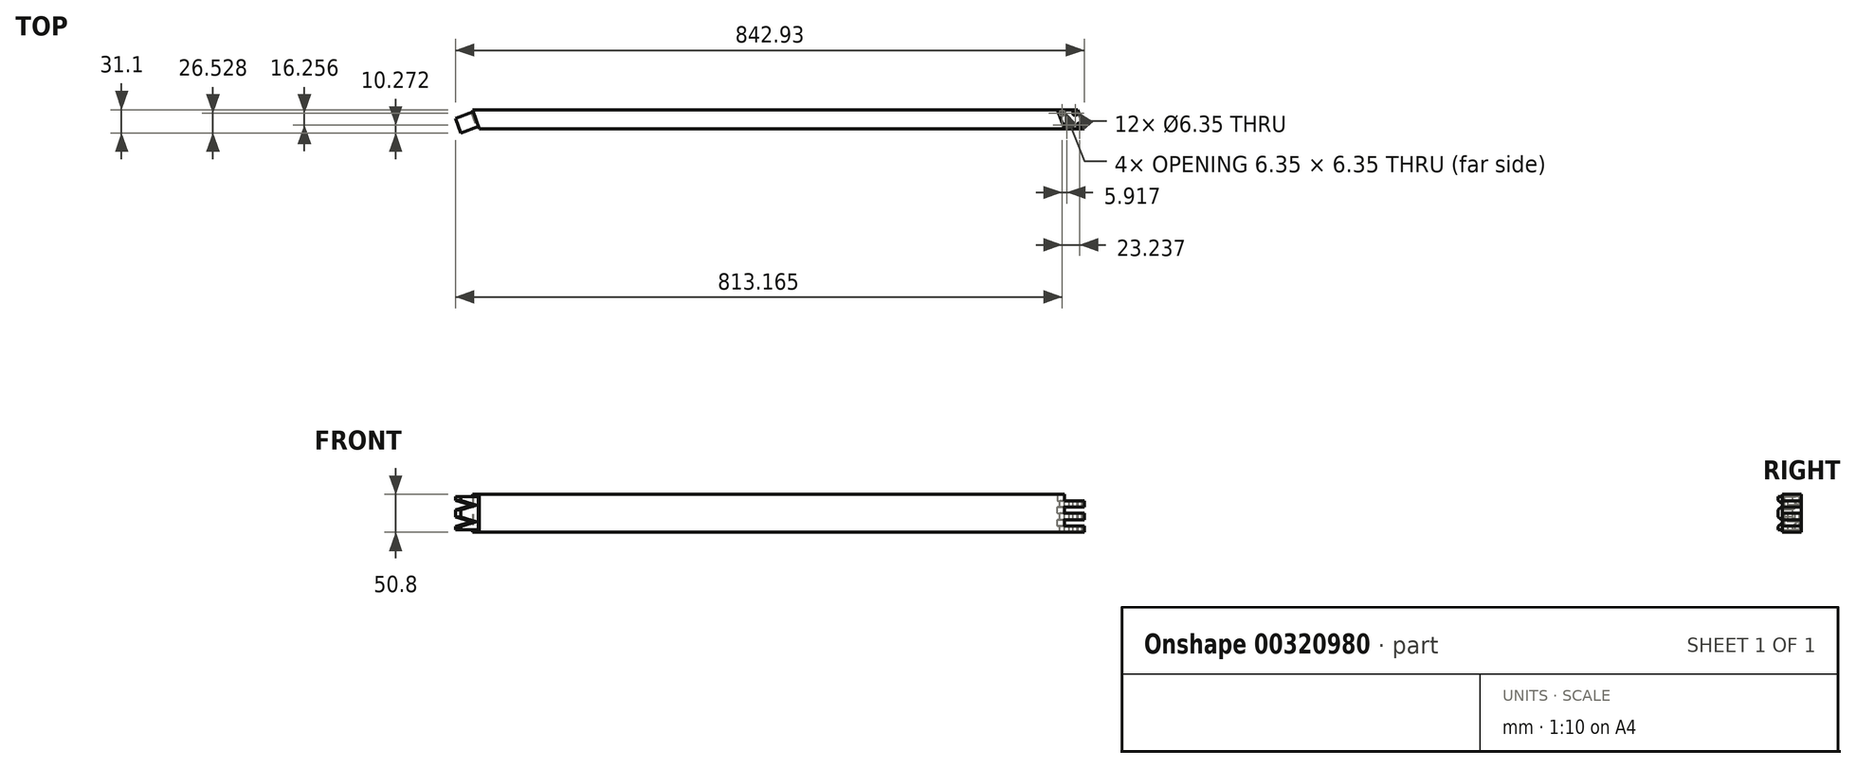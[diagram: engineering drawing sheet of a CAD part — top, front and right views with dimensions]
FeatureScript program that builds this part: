
annotation { "Feature Type Name" : "Feature", "Feature Type Description" : "" }
export const myFeature = defineFeature(function(context is Context, id is Id, definition is map)
    precondition{}
    {
        {
            var Q0;
            Q0=qCreatedBy(makeId("Top.planeOp"),FACE);
            var sketch = newSketch(context, id + "F0", { "sketchPlane" : qUnion([Q0])});
            skLineSegment(sketch, "E0", {"start": v(-414.7, 12.7) * mm, "end": v(-405.45, -12.7) * mm});
            skLineSegment(sketch, "E1", {"start": v(-405.45, -12.7) * mm, "end": v(405.45, -12.7) * mm});
            skLineSegment(sketch, "E2", {"start": v(405.45, -12.7) * mm, "end": v(396.2, 12.7) * mm});
            skLineSegment(sketch, "E3", {"start": v(396.2, 12.7) * mm, "end": v(-414.7, 12.7) * mm});
            skLineSegment(sketch, "E4", {"start": v(369.18, 12.7) * mm, "end": v(378.42, -12.7) * mm, "construction": true});
            skLineSegment(sketch, "E5", {"start": v(-387.67, 12.7) * mm, "end": v(-378.42, -12.7) * mm, "construction": true});
            skSolve(sketch);
        }
        {
            var Q0;
            Q0=makeQuery(id+"F0.imprint","IMPRINT",FACE,{"disambiguationData":[TD([[makeQuery(id+"F0.imprint","IMPRINT",EDGE,{"derivedFrom":sQuery(id+"F0.wireOp",EDGE,"E0")}),1.0]])]});
            extrude(context, id + "F1", {"entities" : qUnion([Q0]), "depth" : 50.8 * mm});
        }
        {
            var Q0;
            Q0=makeQuery(id+"F1.opExtrude","SWEPT_FACE",FACE,{"disambiguationData":[OSD([sQuery(id+"F0.wireOp",EDGE,"E3")])]});
            var sketch = newSketch(context, id + "F2", { "sketchPlane" : qUnion([Q0])});
            skLineSegment(sketch, "E6", {"start": v(-396.2, 8.47) * mm, "end": v(-369.16, 8.47) * mm});
            skLineSegment(sketch, "E7", {"start": v(-369.16, 8.47) * mm, "end": v(-369.16, 0) * mm});
            skLineSegment(sketch, "E8", {"start": v(-369.16, 0) * mm, "end": v(-396.2, 0) * mm});
            skLineSegment(sketch, "E9", {"start": v(-396.2, 0) * mm, "end": v(-396.2, 8.47) * mm});
            skLineSegment(sketch, "E10", {"start": v(-396.2, 16.93) * mm, "end": v(-369.16, 16.93) * mm});
            skLineSegment(sketch, "E11", {"start": v(-369.16, 16.93) * mm, "end": v(-369.16, 25.4) * mm});
            skLineSegment(sketch, "E12", {"start": v(-369.16, 25.4) * mm, "end": v(-396.2, 25.4) * mm});
            skLineSegment(sketch, "E13", {"start": v(-396.2, 25.4) * mm, "end": v(-396.2, 16.93) * mm});
            skLineSegment(sketch, "E14", {"start": v(-396.2, 33.87) * mm, "end": v(-369.16, 33.87) * mm});
            skLineSegment(sketch, "E15", {"start": v(-369.16, 33.87) * mm, "end": v(-369.16, 42.33) * mm});
            skLineSegment(sketch, "E16", {"start": v(-369.16, 42.33) * mm, "end": v(-396.2, 42.33) * mm});
            skLineSegment(sketch, "E17", {"start": v(-396.2, 42.33) * mm, "end": v(-396.2, 33.87) * mm});
            skLineSegment(sketch, "E18", {"start": v(-369.16, 8.47) * mm, "end": v(-369.16, 16.93) * mm});
            skLineSegment(sketch, "E19", {"start": v(-369.16, 25.4) * mm, "end": v(-369.16, 33.87) * mm});
            skLineSegment(sketch, "E20", {"start": v(-369.16, 50.8) * mm, "end": v(-369.16, 42.33) * mm});
            skSolve(sketch);
        }
        {
            var Q0;
            {var subQ0=sQuery(id+"F2.wireOp",EDGE,"E6");Q0=makeQuery(id+"F2.imprint","IMPRINT",FACE,{"disambiguationData":[TD([[makeQuery(id+"F2.imprint","IMPRINT",EDGE,{"derivedFrom":subQ0}),1.0]])]});}
            var Q1;
            {var subQ0=sQuery(id+"F2.wireOp",EDGE,"E12");Q1=makeQuery(id+"F2.imprint","IMPRINT",FACE,{"disambiguationData":[TD([[makeQuery(id+"F2.imprint","IMPRINT",EDGE,{"derivedFrom":subQ0}),-1.0]])]});}
            var Q2;
            {var subQ0=sQuery(id+"F2.wireOp",EDGE,"E16");Q2=makeQuery(id+"F2.imprint","IMPRINT",FACE,{"disambiguationData":[TD([[makeQuery(id+"F2.imprint","IMPRINT",EDGE,{"derivedFrom":subQ0}),-1.0]])]});}
            var Q3;
            Q3=makeQuery(id+"F1.opExtrude","CAP_EDGE",EDGE,{"disambiguationData":[OSD([sQuery(id+"F0.wireOp",EDGE,"E2")])],"isStart":false});
            sweep(context, id + "F3", {"operationType" : NewBodyOperationType.REMOVE, "profiles" : qUnion([Q0, Q1, Q2]), "path" : qUnion([Q3])});
        }
        {
            var Q0;
            Q0=makeQuery(id+"F1.opExtrude","CAP_FACE",FACE,{"disambiguationData":[OSD([sQuery(id+"F0.wireOp",EDGE,"E0"),sQuery(id+"F0.wireOp",EDGE,"E1"),sQuery(id+"F0.wireOp",EDGE,"E2"),sQuery(id+"F0.wireOp",EDGE,"E3")])],"isStart":false});
            var sketch = newSketch(context, id + "F4", { "sketchPlane" : qUnion([Q0])});
            skLineSegment(sketch, "E21", {"start": v(-405.45, -12.7) * mm, "end": v(-429.32, -21.39) * mm});
            skSolve(sketch);
        }
        {
            var Q0;
            Q0=makeQuery(id+"F1.opExtrude","SWEPT_FACE",FACE,{"disambiguationData":[OSD([sQuery(id+"F0.wireOp",EDGE,"E0")])]});
            var sketch = newSketch(context, id + "F5", { "sketchPlane" : qUnion([Q0])});
            skLineSegment(sketch, "E22.bottom", {"start": v(-129.91, 47.62) * mm, "end": v(-150.6, 47.62) * mm});
            skLineSegment(sketch, "E22.top", {"start": v(-129.91, 3.18) * mm, "end": v(-150.6, 3.18) * mm});
            skLineSegment(sketch, "E22.left", {"start": v(-129.91, 47.62) * mm, "end": v(-129.91, 3.18) * mm});
            skLineSegment(sketch, "E22.right", {"start": v(-150.6, 47.62) * mm, "end": v(-150.6, 3.18) * mm});
            skSolve(sketch);
        }
        {
            var Q0;
            Q0=makeQuery(id+"F5.imprint","IMPRINT",FACE,{"disambiguationData":[TD([[makeQuery(id+"F5.imprint","IMPRINT",EDGE,{"derivedFrom":sQuery(id+"F5.wireOp",EDGE,"E22.bottom")}),1.0]])]});
            var Q1;
            Q1=sQuery(id+"F4.wireOp",EDGE,"E21");
            sweep(context, id + "F6", {"operationType" : NewBodyOperationType.ADD, "profiles" : qUnion([Q0]), "path" : qUnion([Q1])});
        }
        {
            var Q0;
            Q0=makeQuery(id+"F6.opSweep","SWEPT_FACE",FACE,{"disambiguationData":[OSD([sQuery(id+"F4.wireOp",EDGE,"E21"),sQuery(id+"F5.wireOp",EDGE,"E22.left")])]});
            var sketch = newSketch(context, id + "F7", { "sketchPlane" : qUnion([Q0])});
            skLineSegment(sketch, "E23", {"start": v(-410.74, 42.86) * mm, "end": v(-388.52, 36.51) * mm});
            skLineSegment(sketch, "E24", {"start": v(-388.52, 36.51) * mm, "end": v(-410.74, 30.16) * mm});
            skLineSegment(sketch, "E25", {"start": v(-410.74, 30.16) * mm, "end": v(-410.74, 42.86) * mm});
            skLineSegment(sketch, "E26", {"start": v(-410.74, 25.4) * mm, "end": v(-382.98, 25.4) * mm, "construction": true});
            skPoint(sketch, "E26.endSnap0", {"position": v(-385.34, 25.4) * mm});
            skLineSegment(sketch, "E27.MirrorCS", {"start": v(-410.74, 20.64) * mm, "end": v(-410.74, 7.94) * mm});
            skLineSegment(sketch, "E28.MirrorCS", {"start": v(-388.52, 14.29) * mm, "end": v(-410.74, 20.64) * mm});
            skLineSegment(sketch, "E29.MirrorCS", {"start": v(-410.74, 7.94) * mm, "end": v(-388.52, 14.29) * mm});
            skSolve(sketch);
        }
        {
            var Q0;
            Q0=makeQuery(id+"F7.imprint","IMPRINT",FACE,{"disambiguationData":[TD([[makeQuery(id+"F7.imprint","IMPRINT",EDGE,{"derivedFrom":sQuery(id+"F7.wireOp",EDGE,"E23")}),-1.0]])]});
            var Q1;
            Q1=makeQuery(id+"F7.imprint","IMPRINT",FACE,{"disambiguationData":[TD([[makeQuery(id+"F7.imprint","IMPRINT",EDGE,{"derivedFrom":sQuery(id+"F7.wireOp",EDGE,"E27.MirrorCS")}),-1.0]])]});
            extrude(context, id + "F8", {"entities" : qUnion([Q0, Q1]), "operationType" : NewBodyOperationType.REMOVE, "endBound" : BoundingType.THROUGH_ALL, "oppositeDirection" : true, "depth" : 25.4 * mm});
        }
        {
            var Q0;
            Q0=makeQuery(id+"F3.boolean.opBoolean","COPY",FACE,{"derivedFrom":makeQuery(id+"F3.opSweep","SWEPT_FACE",FACE,{"disambiguationData":[OSD([sQuery(id+"F0.wireOp",EDGE,"E2"),sQuery(id+"F2.wireOp",EDGE,"E16")])]})});
            var sketch = newSketch(context, id + "F9", { "sketchPlane" : qUnion([Q0])});
            skLineSegment(sketch, "E30.0", {"start": v(398.92, -8.13) * mm, "end": v(393, 8.13) * mm, "construction": true});
            skLineSegment(sketch, "E30.1", {"start": v(381.6, -8.13) * mm, "end": v(398.92, -8.13) * mm, "construction": true});
            skLineSegment(sketch, "E30.2", {"start": v(375.69, 8.13) * mm, "end": v(381.6, -8.13) * mm, "construction": true});
            skLineSegment(sketch, "E30.3", {"start": v(393, 8.13) * mm, "end": v(375.69, 8.13) * mm, "construction": true});
            skCircle(sketch, "E31", {"center": v(393, 8.13) * mm, "radius": 3.18 * mm});
            skCircle(sketch, "E32", {"center": v(375.69, 8.13) * mm, "radius": 3.18 * mm});
            skCircle(sketch, "E33", {"center": v(381.6, -8.13) * mm, "radius": 3.18 * mm});
            skCircle(sketch, "E34", {"center": v(398.92, -8.13) * mm, "radius": 3.18 * mm});
            skSolve(sketch);
        }
        {
            var Q0;
            Q0=makeQuery(id+"F9.imprint","IMPRINT",FACE,{"disambiguationData":[TD([[makeQuery(id+"F9.imprint","IMPRINT",EDGE,{"derivedFrom":sQuery(id+"F9.wireOp",EDGE,"E31")}),1.0]])]});
            var Q1;
            Q1=makeQuery(id+"F9.imprint","IMPRINT",FACE,{"disambiguationData":[TD([[makeQuery(id+"F9.imprint","IMPRINT",EDGE,{"derivedFrom":sQuery(id+"F9.wireOp",EDGE,"E32")}),1.0]])]});
            var Q2;
            Q2=makeQuery(id+"F9.imprint","IMPRINT",FACE,{"disambiguationData":[TD([[makeQuery(id+"F9.imprint","IMPRINT",EDGE,{"derivedFrom":sQuery(id+"F9.wireOp",EDGE,"E33")}),1.0]])]});
            var Q3;
            Q3=makeQuery(id+"F9.imprint","IMPRINT",FACE,{"disambiguationData":[TD([[makeQuery(id+"F9.imprint","IMPRINT",EDGE,{"derivedFrom":sQuery(id+"F9.wireOp",EDGE,"E34")}),1.0]])]});
            extrude(context, id + "F10", {"entities" : qUnion([Q0, Q1, Q2, Q3]), "operationType" : NewBodyOperationType.REMOVE, "endBound" : BoundingType.THROUGH_ALL, "oppositeDirection" : true, "depth" : 25.4 * mm});
        }
    });
